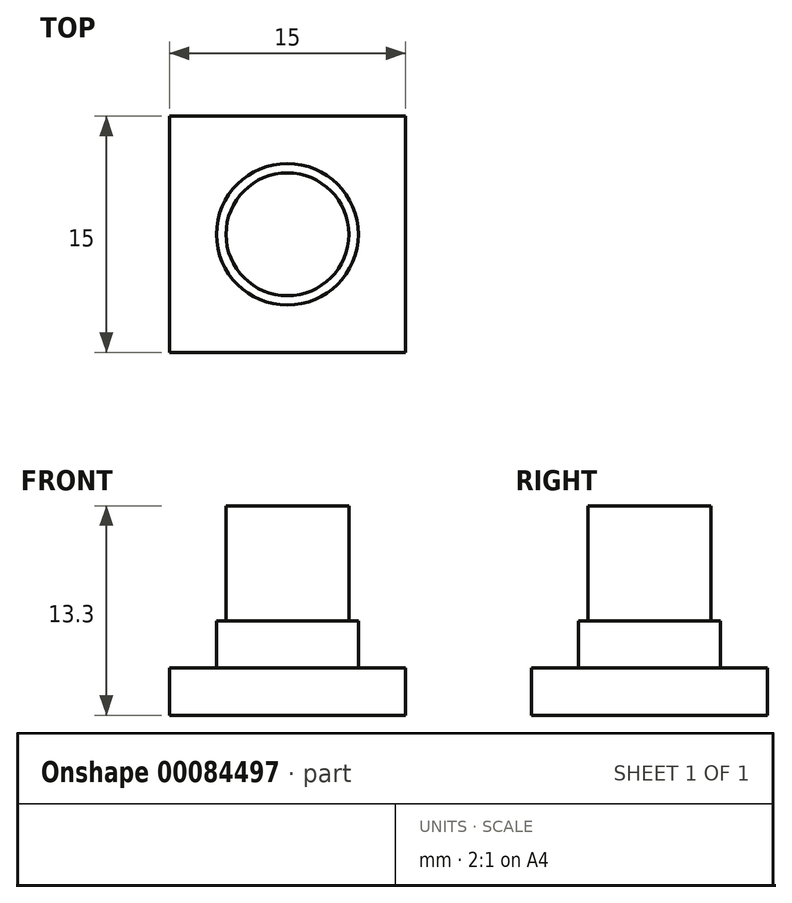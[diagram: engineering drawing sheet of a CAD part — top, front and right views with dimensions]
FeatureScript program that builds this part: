
annotation { "Feature Type Name" : "Feature", "Feature Type Description" : "" }
export const myFeature = defineFeature(function(context is Context, id is Id, definition is map)
    precondition{}
    {
        {
            var Q0;
            Q0=qCreatedBy(makeId("Top.planeOp"),FACE);
            var sketch = newSketch(context, id + "F0", { "sketchPlane" : qUnion([Q0])});
            skLineSegment(sketch, "E0.bottom", {"start": v(7.5, -7.5) * mm, "end": v(-7.5, -7.5) * mm});
            skLineSegment(sketch, "E0.top", {"start": v(7.5, 7.5) * mm, "end": v(-7.5, 7.5) * mm});
            skLineSegment(sketch, "E0.left", {"start": v(7.5, -7.5) * mm, "end": v(7.5, 7.5) * mm});
            skLineSegment(sketch, "E0.right", {"start": v(-7.5, -7.5) * mm, "end": v(-7.5, 7.5) * mm});
            skPoint(sketch, "E0.middle", {"position": v(0, 0) * mm});
            skPoint(sketch, "E1", {"position": v(0, 7.5) * mm});
            skPoint(sketch, "E2", {"position": v(0, -7.5) * mm});
            skCircle(sketch, "E3", {"center": v(0, 0) * mm, "radius": 4.5 * mm});
            skCircle(sketch, "E4", {"center": v(0, 0) * mm, "radius": 3.9 * mm});
            skSolve(sketch);
        }
        {
            var Q0;
            Q0=makeQuery(id+"F0.imprint","IMPRINT",FACE,{"disambiguationData":[TD([[makeQuery(id+"F0.imprint","IMPRINT",EDGE,{"derivedFrom":sQuery(id+"F0.wireOp",EDGE,"E0.bottom")}),-1.0]])]});
            extrude(context, id + "F1", {"entities" : qUnion([Q0]), "depth" : 3 * mm});
        }
        {
            var Q0;
            Q0=makeQuery(id+"F0.imprint","IMPRINT",FACE,{"disambiguationData":[TD([[makeQuery(id+"F0.imprint","IMPRINT",EDGE,{"derivedFrom":sQuery(id+"F0.wireOp",EDGE,"E3")}),1.0]])]});
            extrude(context, id + "F2", {"entities" : qUnion([Q0]), "operationType" : NewBodyOperationType.ADD, "depth" : 6 * mm});
        }
        {
            var Q0;
            Q0=makeQuery(id+"F0.imprint","IMPRINT",FACE,{"disambiguationData":[TD([[makeQuery(id+"F0.imprint","IMPRINT",EDGE,{"derivedFrom":sQuery(id+"F0.wireOp",EDGE,"E4")}),1.0]])]});
            extrude(context, id + "F3", {"entities" : qUnion([Q0]), "operationType" : NewBodyOperationType.ADD, "depth" : 13.3 * mm});
        }
    });
